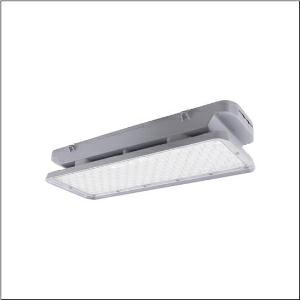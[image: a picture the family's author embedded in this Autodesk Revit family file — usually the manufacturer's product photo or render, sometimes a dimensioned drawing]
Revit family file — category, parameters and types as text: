
# Revit family: highbay_21-s_51hk41da4jca
name_source: partatom
category: Lighting Fixtures
units: mm (PartAtom-declared; Revit-internal decimal feet)

## family parameters
Cut with Voids When Loaded = No
Host = Face
Light Source = No
Part Type = Normal
Room Calculation Point = No
Round Connector Dimension = Use Diameter
Shared = No

## types (1)
- Highbay 21-S (1 x LED, 19100 lm, 107 W, 4000K)
    Apparent Load = 107 VA
    CIE Flux Codes = 87 97 99 100 100
    Color Rendering = 80
    Color Temperature = 4000K
    Default Elevation = 1800 mm
    Description = Highbay 21-S, LED high bay luminaire, primary light control with lens, of PC, primary optical cover: cover panel, light emission: direct distribution, primary light characteristic: symmetric, installation type: suspended mounting, surface-mounted, LED, rated luminous flux: 19.100lm, luminous efficacy: 159lm/W, light colour: 840, colour temperature: 4000K, control gear: ECG DALI, with terminal, 5-pole, max. 2.5mm², mains connection: 220..240V, AC, 50Hz, rated input power: 120W, housing, of diecast aluminium, coated, grey, length: 471mm, width: 172mm, height: 87mm, protection rating (complete): IP66, insulation class (complete): insulation class I (protective earthing), certification: CE, ENEC, UKCA, protection symbol: D, impact resistance: IK08, permissible operating ambient temperature: -30..+55°C, corresponds to IFS (International Featured Standards) requirements for safety and quality in the food industry, LABS conformity tested according to VDMA 24364:2018-05, packaging unit: 1 piece
    Height = 89 mm
    Lamp = 1 x LED
    Lamp Light Flux = 19100 lm
    Lamp Power = 107 W
    Lamp count = 1
    Length = 471 mm
    Luminous efficacy = 179 lm/W
    Manufacturer = Siteco
    ModVariant = No
    Model = 51HK41DA4JCA
    Mounting Place = Ceiling
    Mounting Type = Pendant
    Number of Poles = 1
    OnlyDefault = Yes
    Power Factor = 1
    Product Name = Highbay 21-S
    Product group = LED high bay luminaire
    ProductGroupID = 903
    Protection Class = Protection class I
    Protection Degree = IP 66
    RLX_Detail_Level = 1
    RLX_Emergency_Light_Flux = 0 lm
    RLX_Emergency_Type = 0
    RLX_Emergency_Type_DB = No
    RlxData = <blob elided: 21537 chars, md5=7bd43638>
    Socket = socket
    Standby Power = 0 W
    System Light Flux = 19100 lm
    System Power = 107 W
    Type Comments = Product without accessories
    Type Image = l_1276526.jpg
    URL = http://relux.com
    VarID = ---
    Voltage = 0 V
    Weight = 0.00 kg
    Width = 172 mm

## geometry (parser evidence)
native form markers: Blend x4, Sweep x11
no freeform markers — native parametric forms only
